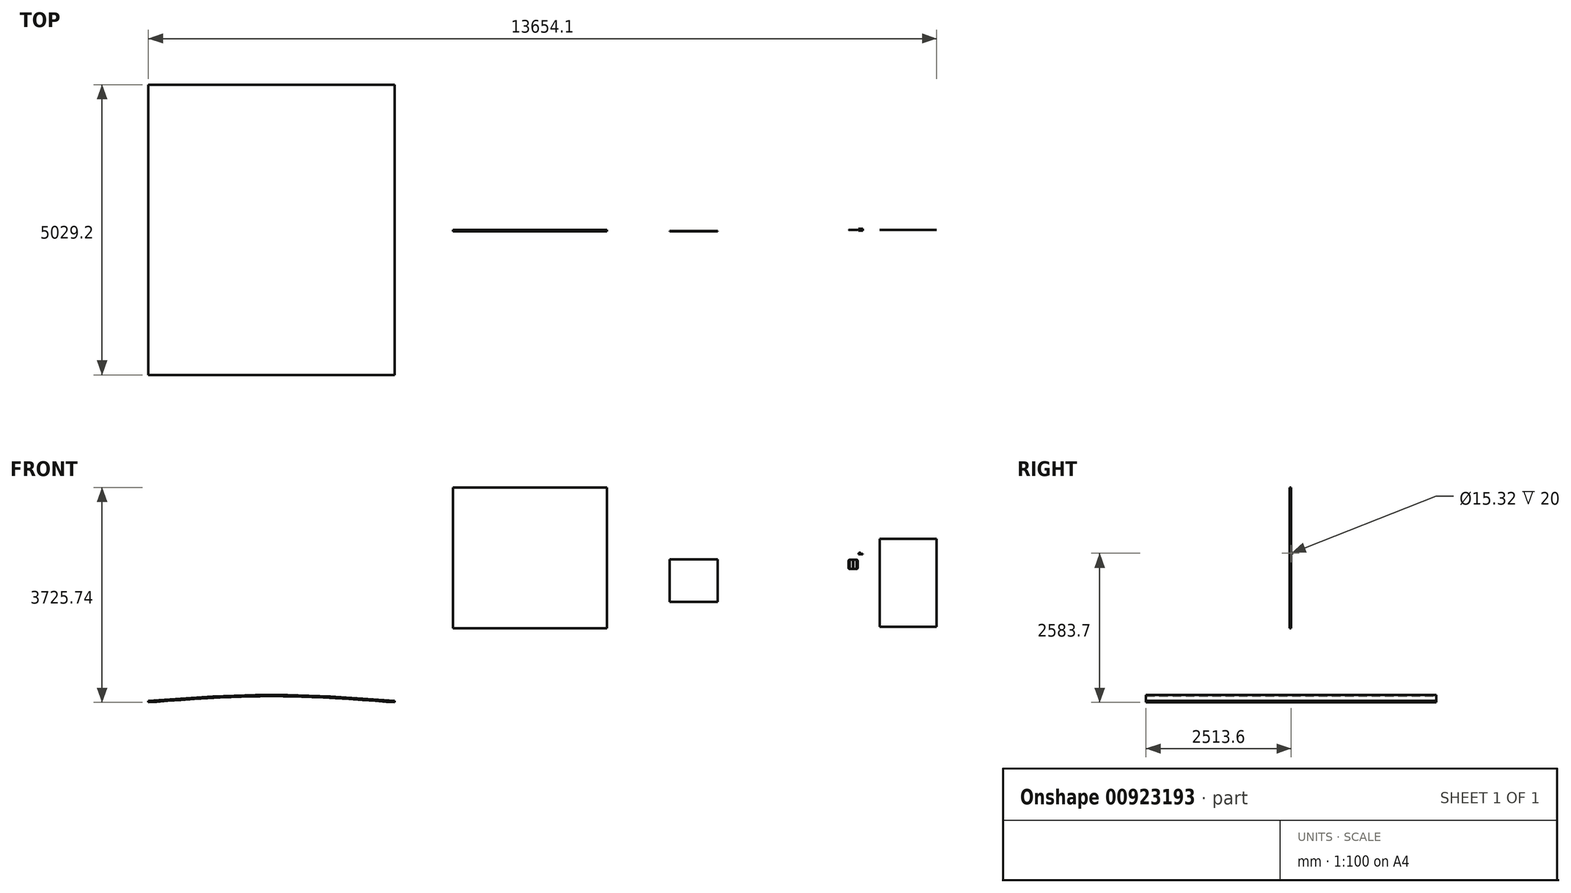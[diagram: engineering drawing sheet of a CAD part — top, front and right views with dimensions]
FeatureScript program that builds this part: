
annotation { "Feature Type Name" : "Feature", "Feature Type Description" : "" }
export const myFeature = defineFeature(function(context is Context, id is Id, definition is map)
    precondition{}
    {
        {
            var Q0;
            Q0=qCreatedBy(makeId("Front.planeOp"),FACE);
            var sketch = newSketch(context, id + "F0", { "sketchPlane" : qUnion([Q0])});
            skLineSegment(sketch, "E0", {"start": v(1286.74, 1046.2) * mm, "end": v(2276.74, 1046.2) * mm});
            skLineSegment(sketch, "E1", {"start": v(2276.74, -476.4) * mm, "end": v(1286.74, -476.4) * mm});
            skLineSegment(sketch, "E2", {"start": v(1286.74, 1046.2) * mm, "end": v(1286.74, -476.4) * mm});
            skLineSegment(sketch, "E3", {"start": v(2276.74, 1046.2) * mm, "end": v(2276.74, -476.4) * mm});
            skSolve(sketch);
        }
        {
            var Q0;
            Q0=makeQuery(id+"F0.imprint","IMPRINT",FACE,{"disambiguationData":[TD([[makeQuery(id+"F0.imprint","IMPRINT",EDGE,{"derivedFrom":sQuery(id+"F0.wireOp",EDGE,"E0")}),-1.0]])]});
            var sketch = newSketch(context, id + "F1", { "sketchPlane" : qUnion([Q0])});
            skLineSegment(sketch, "E4.bottom", {"start": v(766.3, 681.77) * mm, "end": v(892.3, 681.77) * mm});
            skLineSegment(sketch, "E4.top", {"start": v(766.3, 525.77) * mm, "end": v(892.3, 525.77) * mm});
            skLineSegment(sketch, "E4.left", {"start": v(751.3, 666.77) * mm, "end": v(751.3, 540.77) * mm});
            skLineSegment(sketch, "E4.right", {"start": v(907.3, 666.77) * mm, "end": v(907.3, 540.77) * mm});
            skPoint(sketch, "E5.visualSharp", {"position": v(751.3, 681.77) * mm});
            skArc(sketch, "E5.filletArc", {"start": v(766.3, 681.77) * mm, "mid": v(755.7, 677.38) * mm, "end": v(751.3, 666.77) * mm});
            skPoint(sketch, "E6.visualSharp", {"position": v(907.3, 681.77) * mm});
            skArc(sketch, "E6.filletArc", {"start": v(907.3, 666.77) * mm, "mid": v(902.9, 677.38) * mm, "end": v(892.3, 681.77) * mm});
            skPoint(sketch, "E7.visualSharp", {"position": v(907.3, 525.77) * mm});
            skArc(sketch, "E7.filletArc", {"start": v(892.3, 525.77) * mm, "mid": v(902.9, 530.16) * mm, "end": v(907.3, 540.77) * mm});
            skPoint(sketch, "E8.visualSharp", {"position": v(751.3, 525.77) * mm});
            skArc(sketch, "E8.filletArc", {"start": v(751.3, 540.77) * mm, "mid": v(755.7, 530.16) * mm, "end": v(766.3, 525.77) * mm});
            skLineSegment(sketch, "E9.bottom", {"start": v(3038.85, 81858.35) * mm, "end": v(2869.38, 81858.35) * mm});
            skLineSegment(sketch, "E9.top", {"start": v(3038.85, 72650.5) * mm, "end": v(2869.38, 72650.5) * mm});
            skLineSegment(sketch, "E9.left", {"start": v(3038.85, 81858.35) * mm, "end": v(3038.85, 72650.5) * mm});
            skLineSegment(sketch, "E9.right", {"start": v(2869.38, 81858.35) * mm, "end": v(2869.38, 72650.5) * mm});
            skSolve(sketch);
        }
        {
            var Q0;
            Q0=makeQuery(id+"F0.imprint","IMPRINT",FACE,{"disambiguationData":[TD([[makeQuery(id+"F0.imprint","IMPRINT",EDGE,{"derivedFrom":sQuery(id+"F0.wireOp",EDGE,"E0")}),-1.0]])]});
            extrude(context, id + "F2", {"entities" : qUnion([Q0]), "depth" : 1 * mm, "offsetDistance" : 25 * mm});
        }
        {
            var Q0;
            Q0=makeQuery(id+"F1.imprint","IMPRINT",FACE,{"disambiguationData":[TD([[makeQuery(id+"F1.imprint","IMPRINT",EDGE,{"derivedFrom":sQuery(id+"F1.wireOp",EDGE,"E4.bottom")}),-1.0]])]});
            extrude(context, id + "F3", {"entities" : qUnion([Q0]), "depth" : 1 * mm, "offsetDistance" : 25 * mm});
        }
        {
            var Q0;
            Q0=makeQuery(id+"F3.opExtrude","CAP_FACE",FACE,{"disambiguationData":[OSD([sQuery(id+"F1.wireOp",EDGE,"E4.bottom"),sQuery(id+"F1.wireOp",EDGE,"E4.top"),sQuery(id+"F1.wireOp",EDGE,"E4.left"),sQuery(id+"F1.wireOp",EDGE,"E4.right"),sQuery(id+"F1.wireOp",EDGE,"E5.filletArc"),sQuery(id+"F1.wireOp",EDGE,"E6.filletArc"),sQuery(id+"F1.wireOp",EDGE,"E7.filletArc"),sQuery(id+"F1.wireOp",EDGE,"E8.filletArc")])],"isStart":false});
            var sketch = newSketch(context, id + "F4", { "sketchPlane" : qUnion([Q0])});
            skLineSegment(sketch, "E10.bottom", {"start": v(1068.35, 691.33) * mm, "end": v(1072.64, 691.33) * mm});
            skLineSegment(sketch, "E10.top", {"start": v(1068.35, 535.33) * mm, "end": v(1072.64, 535.33) * mm});
            skLineSegment(sketch, "E10.left", {"start": v(1068.35, 691.33) * mm, "end": v(1068.35, 535.33) * mm});
            skLineSegment(sketch, "E10.right", {"start": v(1072.64, 691.33) * mm, "end": v(1072.64, 535.33) * mm});
            skLineSegment(sketch, "E11.bottom", {"start": v(1040.3, 699.13) * mm, "end": v(1044.6, 699.13) * mm});
            skLineSegment(sketch, "E11.top", {"start": v(1040.3, 543.13) * mm, "end": v(1044.6, 543.13) * mm});
            skLineSegment(sketch, "E11.left", {"start": v(1040.3, 699.13) * mm, "end": v(1040.3, 543.13) * mm});
            skLineSegment(sketch, "E11.right", {"start": v(1044.6, 699.13) * mm, "end": v(1044.6, 543.13) * mm});
            skLineSegment(sketch, "E12.bottom", {"start": v(997.94, 678.37) * mm, "end": v(1002.23, 678.37) * mm});
            skLineSegment(sketch, "E12.top", {"start": v(997.94, 522.37) * mm, "end": v(1002.23, 522.37) * mm});
            skLineSegment(sketch, "E12.left", {"start": v(997.94, 678.37) * mm, "end": v(997.94, 522.37) * mm});
            skLineSegment(sketch, "E12.right", {"start": v(1002.23, 678.37) * mm, "end": v(1002.23, 522.37) * mm});
            skSolve(sketch);
        }
        {
            var Q0;
            Q0=makeQuery(id+"F4.imprint","IMPRINT",FACE,{"disambiguationData":[TD([[makeQuery(id+"F4.imprint","IMPRINT",EDGE,{"derivedFrom":sQuery(id+"F4.wireOp",EDGE,"E10.bottom")}),-1.0]])]});
            var Q1;
            Q1=makeQuery(id+"F4.imprint","IMPRINT",FACE,{"disambiguationData":[TD([[makeQuery(id+"F4.imprint","IMPRINT",EDGE,{"derivedFrom":sQuery(id+"F4.wireOp",EDGE,"E11.bottom")}),-1.0]])]});
            var Q2;
            Q2=makeQuery(id+"F4.imprint","IMPRINT",FACE,{"disambiguationData":[TD([[makeQuery(id+"F4.imprint","IMPRINT",EDGE,{"derivedFrom":sQuery(id+"F4.wireOp",EDGE,"E12.bottom")}),-1.0]])]});
            extrude(context, id + "F5", {"entities" : qUnion([Q0, Q1, Q2]), "depth" : 0.5 * mm, "offsetDistance" : 25 * mm});
        }
        {
            var Q0;
            Q0=makeQuery(id+"F5.opExtrude","SWEPT_BODY",BODY,{"disambiguationData":[OSD([sQuery(id+"F4.wireOp",EDGE,"E12.bottom"),sQuery(id+"F4.wireOp",EDGE,"E12.top"),sQuery(id+"F4.wireOp",EDGE,"E12.left"),sQuery(id+"F4.wireOp",EDGE,"E12.right")])]});
            transform(context, id + "F6", {"entities" : qUnion([Q0]), "transformType" : TransformType.TRANSLATION_3D, "dx" : -232.8 * mm, "dy" : 0 * mm, "dz" : 3.3 * mm, "makeCopy" : false});
        }
        {
            var Q0;
            Q0=makeQuery(id+"F5.opExtrude","SWEPT_BODY",BODY,{"disambiguationData":[OSD([sQuery(id+"F4.wireOp",EDGE,"E12.bottom"),sQuery(id+"F4.wireOp",EDGE,"E12.top"),sQuery(id+"F4.wireOp",EDGE,"E12.left"),sQuery(id+"F4.wireOp",EDGE,"E12.right")])]});
            transform(context, id + "F7", {"entities" : qUnion([Q0]), "transformType" : TransformType.TRANSLATION_3D, "dx" : 6E-4000 * mm, "dy" : 0 * mm, "dz" : 0 * mm, "makeCopy" : false});
        }
        {
            var Q0;
            Q0=makeQuery(id+"F5.opExtrude","SWEPT_BODY",BODY,{"disambiguationData":[OSD([sQuery(id+"F4.wireOp",EDGE,"E12.bottom"),sQuery(id+"F4.wireOp",EDGE,"E12.top"),sQuery(id+"F4.wireOp",EDGE,"E12.left"),sQuery(id+"F4.wireOp",EDGE,"E12.right")])]});
            var Q1;
            Q1=makeQuery(id+"F5.opExtrude","CAP_VERTEX",VERTEX,{"disambiguationData":[OSD([sQuery(id+"F4.wireOp",EDGE,"E12.top"),sQuery(id+"F4.wireOp",EDGE,"E12.left")])],"isStart":false});
            var Q2;
            Q2=makeQuery(id+"F3.opExtrude","CAP_EDGE",EDGE,{"disambiguationData":[OSD([sQuery(id+"F1.wireOp",EDGE,"E4.top")])],"isStart":false});
            transform(context, id + "F8", {"entities" : qUnion([Q0]), "transformType" : TransformType.TRANSLATION_ENTITY, "oppositeDirectionEntity" : false, "transformLine" : qUnion([Q1, Q2]), "makeCopy" : false});
        }
        {
            var Q0;
            Q0=makeQuery(id+"F5.opExtrude","SWEPT_BODY",BODY,{"disambiguationData":[OSD([sQuery(id+"F4.wireOp",EDGE,"E12.bottom"),sQuery(id+"F4.wireOp",EDGE,"E12.top"),sQuery(id+"F4.wireOp",EDGE,"E12.left"),sQuery(id+"F4.wireOp",EDGE,"E12.right")])]});
            var Q1;
            Q1=makeQuery(id+"F5.opExtrude","CAP_VERTEX",VERTEX,{"disambiguationData":[OSD([sQuery(id+"F4.wireOp",EDGE,"E12.bottom"),sQuery(id+"F4.wireOp",EDGE,"E12.right")])],"isStart":true});
            var Q2;
            Q2=makeQuery(id+"F3.opExtrude","CAP_VERTEX",VERTEX,{"disambiguationData":[OSD([sQuery(id+"F1.wireOp",EDGE,"E4.bottom"),sQuery(id+"F1.wireOp",EDGE,"E6.filletArc")])],"isStart":false});
            transform(context, id + "F9", {"entities" : qUnion([Q0]), "transformType" : TransformType.TRANSLATION_ENTITY, "oppositeDirectionEntity" : false, "transformLine" : qUnion([Q1, Q2]), "makeCopy" : false});
        }
        {
            var Q0;
            Q0=makeQuery(id+"F5.opExtrude","SWEPT_BODY",BODY,{"disambiguationData":[OSD([sQuery(id+"F4.wireOp",EDGE,"E11.bottom"),sQuery(id+"F4.wireOp",EDGE,"E11.top"),sQuery(id+"F4.wireOp",EDGE,"E11.left"),sQuery(id+"F4.wireOp",EDGE,"E11.right")])]});
            var Q1;
            Q1=sQuery(id+"F4.wireOp",VERTEX,"E11.bottom.start");
            var Q2;
            Q2=makeQuery(id+"F3.opExtrude","CAP_VERTEX",VERTEX,{"disambiguationData":[OSD([sQuery(id+"F1.wireOp",EDGE,"E4.bottom"),sQuery(id+"F1.wireOp",EDGE,"E5.filletArc")])],"isStart":false});
            transform(context, id + "F10", {"entities" : qUnion([Q0]), "transformType" : TransformType.TRANSLATION_ENTITY, "oppositeDirectionEntity" : false, "transformLine" : qUnion([Q1, Q2]), "makeCopy" : false});
        }
        {
            var Q0;
            Q0=sQuery(id+"F4.wireOp",EDGE,"E10.bottom");
            cPoint(context, id + "F11", {"entities" : qUnion([Q0]), "parameter" : 0.5});
        }
        {
            var Q0;
            Q0=makeQuery(id+"F3.opExtrude","CAP_EDGE",EDGE,{"disambiguationData":[OSD([sQuery(id+"F1.wireOp",EDGE,"E4.bottom")])],"isStart":false});
            cPoint(context, id + "F12", {"entities" : qUnion([Q0]), "parameter" : 0.5});
        }
        {
            var Q0;
            Q0=makeQuery(id+"F5.opExtrude","SWEPT_BODY",BODY,{"disambiguationData":[OSD([sQuery(id+"F4.wireOp",EDGE,"E10.bottom"),sQuery(id+"F4.wireOp",EDGE,"E10.top"),sQuery(id+"F4.wireOp",EDGE,"E10.left"),sQuery(id+"F4.wireOp",EDGE,"E10.right")])]});
            var Q1;
            Q1=qCreatedBy(id+"F11",VERTEX);
            var Q2;
            Q2=qCreatedBy(id+"F12",VERTEX);
            transform(context, id + "F13", {"entities" : qUnion([Q0]), "transformType" : TransformType.TRANSLATION_ENTITY, "oppositeDirectionEntity" : false, "transformLine" : qUnion([Q1, Q2]), "makeCopy" : false});
        }
        {
            var Q0;
            Q0=makeQuery(id+"F2.opExtrude","CAP_FACE",FACE,{"disambiguationData":[OSD([sQuery(id+"F0.wireOp",EDGE,"E0"),sQuery(id+"F0.wireOp",EDGE,"E1"),sQuery(id+"F0.wireOp",EDGE,"E2"),sQuery(id+"F0.wireOp",EDGE,"E3")])],"isStart":false});
            var sketch = newSketch(context, id + "F14", { "sketchPlane" : qUnion([Q0])});
            skLineSegment(sketch, "E13.bottom", {"start": v(919.16, 786.05) * mm, "end": v(997.16, 786.05) * mm});
            skLineSegment(sketch, "E13.top", {"start": v(919.16, 776.05) * mm, "end": v(997.16, 776.05) * mm});
            skLineSegment(sketch, "E13.left", {"start": v(919.16, 786.05) * mm, "end": v(919.16, 776.05) * mm});
            skLineSegment(sketch, "E13.right", {"start": v(997.16, 786.05) * mm, "end": v(997.16, 776.05) * mm});
            skPoint(sketch, "E14.oppositeSnap0", {"position": v(958.16, 786.05) * mm});
            skLineSegment(sketch, "E14.bottom", {"start": v(997.16, 786.05) * mm, "end": v(958.16, 786.05) * mm});
            skLineSegment(sketch, "E14.top", {"start": v(997.16, 803.85) * mm, "end": v(958.16, 803.85) * mm});
            skLineSegment(sketch, "E14.left", {"start": v(997.16, 786.05) * mm, "end": v(997.16, 803.85) * mm});
            skLineSegment(sketch, "E14.right", {"start": v(958.16, 786.05) * mm, "end": v(958.16, 803.85) * mm});
            skLineSegment(sketch, "E15.bottom", {"start": v(958.16, 794.95) * mm, "end": v(930.77, 794.95) * mm});
            skLineSegment(sketch, "E15.top", {"start": v(958.16, 786.05) * mm, "end": v(930.77, 786.05) * mm});
            skLineSegment(sketch, "E15.left", {"start": v(958.16, 794.95) * mm, "end": v(958.16, 786.05) * mm});
            skLineSegment(sketch, "E15.right", {"start": v(930.77, 794.95) * mm, "end": v(930.77, 786.05) * mm});
            skSolve(sketch);
        }
        {
            var Q0;
            Q0=makeQuery(id+"F14.imprint","IMPRINT",FACE,{"disambiguationData":[TD([[makeQuery(id+"F14.imprint","IMPRINT",EDGE,{"derivedFrom":sQuery(id+"F14.wireOp",EDGE,"E14.bottom")}),-1.0]])]});
            var Q1;
            Q1=makeQuery(id+"F14.imprint","IMPRINT",FACE,{"disambiguationData":[TD([[makeQuery(id+"F14.imprint","IMPRINT",EDGE,{"derivedFrom":sQuery(id+"F14.wireOp",EDGE,"E13.bottom")}),-1.0]])]});
            extrude(context, id + "F15", {"entities" : qUnion([Q0, Q1]), "endBound" : BoundingType.SYMMETRIC, "depth" : 32 * mm, "offsetDistance" : 25 * mm});
        }
        {
            var Q0;
            Q0=makeQuery(id+"F14.imprint","IMPRINT",FACE,{"disambiguationData":[TD([[makeQuery(id+"F14.imprint","IMPRINT",EDGE,{"derivedFrom":sQuery(id+"F14.wireOp",EDGE,"E15.bottom")}),1.0]])]});
            var Q1;
            Q1=sQuery(id+"F14.wireOp",EDGE,"E15.bottom");
            revolve(context, id + "F16", {"surfaceOperationType" : NewSurfaceOperationType.NEW, "entities" : qUnion([Q0]), "axis" : qUnion([Q1]), "revolveType" : RevolveType.ONE_DIRECTION, "angle" : 360 * degree});
        }
        {
            var Q0;
            Q0=makeQuery(id+"F16.opRevolve","SWEPT_FACE",FACE,{"disambiguationData":[OSD([sQuery(id+"F14.wireOp",EDGE,"E15.right")])]});
            var sketch = newSketch(context, id + "F17", { "sketchPlane" : qUnion([Q0])});
            skCircle(sketch, "E16", {"center": v(1, 794.95) * mm, "radius": 7.66 * mm});
            skSolve(sketch);
        }
        {
            var Q0;
            Q0=makeQuery(id+"F17.imprint","IMPRINT",FACE,{"disambiguationData":[TD([[makeQuery(id+"F17.imprint","IMPRINT",EDGE,{"derivedFrom":sQuery(id+"F17.wireOp",EDGE,"E16")}),1.0]])]});
            extrude(context, id + "F18", {"entities" : qUnion([Q0]), "operationType" : NewBodyOperationType.REMOVE, "depth" : -20 * mm, "offsetDistance" : 25 * mm});
        }
        {
            var Q0;
            Q0=qCreatedBy(makeId("Front.planeOp"),FACE);
            var sketch = newSketch(context, id + "F19", { "sketchPlane" : qUnion([Q0])});
            skFitSpline(sketch, "E17", {"points": [v(-11377.35, -1763.42) * mm, v(-9243.75, -1656.23) * mm, v(-7110.15, -1763.42) * mm], "startDerivative": vector(4267.2, 321.56) * mm, "endDerivative": vector(4267.2, -321.56) * mm});
            skFitSpline(sketch, "E18.0", {"points": [v(-11375.44, -1788.75) * mm, v(-11197.64, -1775.35) * mm, v(-10842.12, -1748.56) * mm, v(-10397.92, -1719.27) * mm, v(-10042.67, -1700.86) * mm, v(-9776.3, -1690.2) * mm, v(-9554.38, -1684.45) * mm, v(-9376.86, -1682.05) * mm, v(-9243.75, -1681.42) * mm, v(-9110.63, -1682.05) * mm, v(-8933.12, -1684.45) * mm, v(-8711.2, -1690.2) * mm, v(-8444.82, -1700.86) * mm, v(-8089.58, -1719.27) * mm, v(-7645.38, -1748.56) * mm, v(-7289.86, -1775.35) * mm, v(-7112.06, -1788.75) * mm]});
            skLineSegment(sketch, "E19", {"start": v(-11375.44, -1788.75) * mm, "end": v(-11377.35, -1763.42) * mm});
            skLineSegment(sketch, "E20", {"start": v(-7112.06, -1788.75) * mm, "end": v(-7110.15, -1763.42) * mm});
            skSolve(sketch);
        }
        {
            var Q0;
            Q0=makeQuery(id+"F19.imprint","IMPRINT",FACE,{"disambiguationData":[TD([[makeQuery(id+"F19.imprint","IMPRINT",EDGE,{"derivedFrom":sQuery(id+"F19.wireOp",EDGE,"E17")}),-1.0]])]});
            extrude(context, id + "F20", {"entities" : qUnion([Q0]), "endBound" : BoundingType.SYMMETRIC, "depth" : 5029.2 * mm, "offsetDistance" : 25.4 * mm});
        }
        {
            var Q0;
            Q0=qCreatedBy(makeId("Front.planeOp"),FACE);
            var sketch = newSketch(context, id + "F21", { "sketchPlane" : qUnion([Q0])});
            skLineSegment(sketch, "E21.bottom", {"start": v(-6099.09, 1936.99) * mm, "end": v(-3432.09, 1936.99) * mm});
            skLineSegment(sketch, "E21.top", {"start": v(-6099.09, -501.41) * mm, "end": v(-3432.09, -501.41) * mm});
            skLineSegment(sketch, "E21.left", {"start": v(-6099.09, 1936.99) * mm, "end": v(-6099.09, -501.41) * mm});
            skLineSegment(sketch, "E21.right", {"start": v(-3432.09, 1936.99) * mm, "end": v(-3432.09, -501.41) * mm});
            skSolve(sketch);
        }
        {
            var Q0;
            Q0=makeQuery(id+"F21.imprint","IMPRINT",FACE,{"disambiguationData":[TD([[makeQuery(id+"F21.imprint","IMPRINT",EDGE,{"derivedFrom":sQuery(id+"F21.wireOp",EDGE,"E21.bottom")}),-1.0]])]});
            extrude(context, id + "F22", {"entities" : qUnion([Q0]), "depth" : 25.4 * mm, "offsetDistance" : 25.4 * mm});
        }
        {
            var Q0;
            Q0=makeQuery(id+"F22.opExtrude","CAP_FACE",FACE,{"disambiguationData":[OSD([sQuery(id+"F21.wireOp",EDGE,"E21.bottom"),sQuery(id+"F21.wireOp",EDGE,"E21.top"),sQuery(id+"F21.wireOp",EDGE,"E21.left"),sQuery(id+"F21.wireOp",EDGE,"E21.right")])],"isStart":false});
            var sketch = newSketch(context, id + "F23", { "sketchPlane" : qUnion([Q0])});
            skLineSegment(sketch, "E22.bottom", {"start": v(-2349.2, 689.73) * mm, "end": v(-1518.63, 689.73) * mm});
            skLineSegment(sketch, "E22.top", {"start": v(-2349.2, -46.87) * mm, "end": v(-1518.63, -46.87) * mm});
            skLineSegment(sketch, "E22.left", {"start": v(-2349.2, 689.73) * mm, "end": v(-2349.2, -46.87) * mm});
            skLineSegment(sketch, "E22.right", {"start": v(-1518.63, 689.73) * mm, "end": v(-1518.63, -46.87) * mm});
            skSolve(sketch);
        }
        {
            var Q0;
            Q0=makeQuery(id+"F23.imprint","IMPRINT",FACE,{"disambiguationData":[TD([[makeQuery(id+"F23.imprint","IMPRINT",EDGE,{"derivedFrom":sQuery(id+"F23.wireOp",EDGE,"E22.bottom")}),-1.0]])]});
            extrude(context, id + "F24", {"entities" : qUnion([Q0]), "endBound" : BoundingType.SYMMETRIC, "depth" : 1 * mm, "offsetDistance" : 25.4 * mm});
        }
    });
